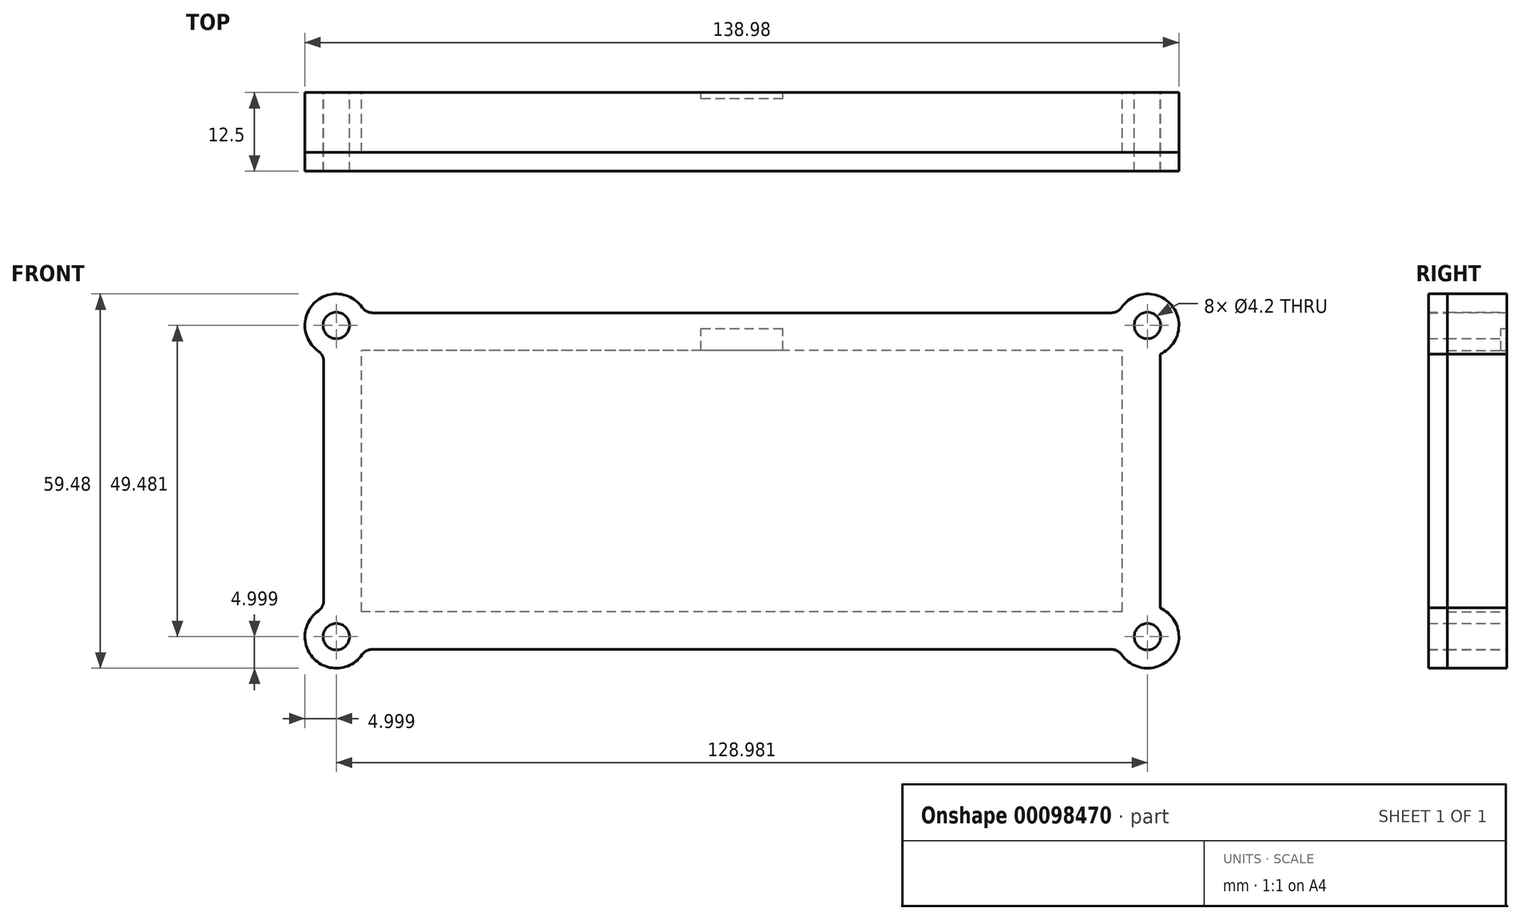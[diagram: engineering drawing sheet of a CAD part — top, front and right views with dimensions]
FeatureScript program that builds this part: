
annotation { "Feature Type Name" : "Feature", "Feature Type Description" : "" }
export const myFeature = defineFeature(function(context is Context, id is Id, definition is map)
    precondition{}
    {
        {
            var Q0;
            Q0=qCreatedBy(makeId("Front.planeOp"),FACE);
            var sketch = newSketch(context, id + "F0", { "sketchPlane" : qUnion([Q0])});
            skLineSegment(sketch, "E0.bottom", {"start": v(60.5, -20.75) * mm, "end": v(-60.5, -20.75) * mm});
            skLineSegment(sketch, "E0.top", {"start": v(60.5, 20.75) * mm, "end": v(-60.5, 20.75) * mm});
            skLineSegment(sketch, "E0.left", {"start": v(60.5, -20.75) * mm, "end": v(60.5, 20.75) * mm});
            skLineSegment(sketch, "E0.right", {"start": v(-60.5, -20.75) * mm, "end": v(-60.5, 20.75) * mm});
            skPoint(sketch, "E0.middle", {"position": v(0, 0) * mm});
            skLineSegment(sketch, "E1.bottom", {"start": v(56.25, 22.8) * mm, "end": v(-56.25, 22.8) * mm, "construction": true});
            skLineSegment(sketch, "E1.top", {"start": v(56.25, -22.8) * mm, "end": v(-56.25, -22.8) * mm, "construction": true});
            skLineSegment(sketch, "E1.left", {"start": v(56.25, 22.8) * mm, "end": v(56.25, -22.8) * mm, "construction": true});
            skLineSegment(sketch, "E1.right", {"start": v(-56.25, 22.8) * mm, "end": v(-56.25, -22.8) * mm, "construction": true});
            skCircle(sketch, "E2", {"center": v(-56.25, 22.8) * mm, "radius": 1 * mm, "construction": true});
            skCircle(sketch, "E3.MirrorC", {"center": v(-56.25, -22.8) * mm, "radius": 1 * mm, "construction": true});
            skCircle(sketch, "E4.MirrorC", {"center": v(56.25, 22.8) * mm, "radius": 1 * mm, "construction": true});
            skCircle(sketch, "E5.MirrorC", {"center": v(56.25, -22.8) * mm, "radius": 1 * mm, "construction": true});
            skLineSegment(sketch, "E6.0", {"start": v(59.91, 26.75) * mm, "end": v(-59.91, 26.75) * mm});
            skLineSegment(sketch, "E6.1", {"start": v(66.5, -20.16) * mm, "end": v(66.5, 20.16) * mm});
            skLineSegment(sketch, "E6.2", {"start": v(59.91, -26.75) * mm, "end": v(-59.91, -26.75) * mm});
            skLineSegment(sketch, "E6.3", {"start": v(-66.5, -20.16) * mm, "end": v(-66.5, 20.16) * mm});
            skLineSegment(sketch, "E7", {"start": v(-66.5, 26.75) * mm, "end": v(-60.5, 20.75) * mm, "construction": true});
            skArc(sketch, "E8", {"start": v(-59.91, 26.75) * mm, "mid": v(-68.03, 28.28) * mm, "end": v(-66.5, 20.16) * mm});
            skCircle(sketch, "E9", {"center": v(-64.5, 24.74) * mm, "radius": 2.1 * mm});
            skArc(sketch, "E10.MirrorCS", {"start": v(59.91, 26.75) * mm, "mid": v(68.03, 28.28) * mm, "end": v(66.5, 20.16) * mm});
            skCircle(sketch, "E11.MirrorC", {"center": v(64.5, 24.74) * mm, "radius": 2.1 * mm});
            skArc(sketch, "E12.MirrorCS", {"start": v(-59.91, -26.75) * mm, "mid": v(-68.03, -28.28) * mm, "end": v(-66.5, -20.16) * mm});
            skCircle(sketch, "E13.MirrorC", {"center": v(-64.5, -24.74) * mm, "radius": 2.1 * mm});
            skArc(sketch, "E14.MirrorCS", {"start": v(59.91, -26.75) * mm, "mid": v(68.03, -28.28) * mm, "end": v(66.5, -20.16) * mm});
            skCircle(sketch, "E15.MirrorC", {"center": v(64.5, -24.74) * mm, "radius": 2.1 * mm});
            skSolve(sketch);
        }
        {
            var Q0;
            Q0 = qSketchRegion(id + "F0", true);
            extrude(context, id + "F1", {"entities" : qUnion([Q0]), "depth" : 9.5 * mm});
        }
        {
            var Q0;
            Q0=makeQuery(id+"F1.opExtrude","SWEPT_EDGE",EDGE,{"disambiguationData":[OSD([sQuery(id+"F0.wireOp",EDGE,"E6.0"),sQuery(id+"F0.wireOp",EDGE,"E8")])]});
            var Q1;
            Q1=makeQuery(id+"F1.opExtrude","SWEPT_EDGE",EDGE,{"disambiguationData":[OSD([sQuery(id+"F0.wireOp",EDGE,"E6.3"),sQuery(id+"F0.wireOp",EDGE,"E8")])]});
            var Q2;
            Q2=makeQuery(id+"F1.opExtrude","SWEPT_EDGE",EDGE,{"disambiguationData":[OSD([sQuery(id+"F0.wireOp",EDGE,"E6.3"),sQuery(id+"F0.wireOp",EDGE,"E12.MirrorCS")])]});
            var Q3;
            Q3=makeQuery(id+"F1.opExtrude","SWEPT_EDGE",EDGE,{"disambiguationData":[OSD([sQuery(id+"F0.wireOp",EDGE,"E6.2"),sQuery(id+"F0.wireOp",EDGE,"E12.MirrorCS")])]});
            var Q4;
            Q4=makeQuery(id+"F1.opExtrude","SWEPT_EDGE",EDGE,{"disambiguationData":[OSD([sQuery(id+"F0.wireOp",EDGE,"E6.2"),sQuery(id+"F0.wireOp",EDGE,"E14.MirrorCS")])]});
            var Q5;
            Q5=makeQuery(id+"F1.opExtrude","SWEPT_EDGE",EDGE,{"disambiguationData":[OSD([sQuery(id+"F0.wireOp",EDGE,"E6.0"),sQuery(id+"F0.wireOp",EDGE,"E10.MirrorCS")])]});
            fillet(context, id + "F2", {"entities" : qUnion([Q0, Q1, Q2, Q3, Q4, Q5]), "radius" : 2 * mm, "tangentPropagation" : true, "allowEdgeOverflow" : false});
        }
        {
            var Q0;
            Q0=makeQuery(id+"F1.opExtrude","CAP_FACE",FACE,{"disambiguationData":[OSD([sQuery(id+"F0.wireOp",EDGE,"E0.bottom"),sQuery(id+"F0.wireOp",EDGE,"E0.top"),sQuery(id+"F0.wireOp",EDGE,"E0.left"),sQuery(id+"F0.wireOp",EDGE,"E0.right"),sQuery(id+"F0.wireOp",EDGE,"E2"),sQuery(id+"F0.wireOp",EDGE,"E3.MirrorC"),sQuery(id+"F0.wireOp",EDGE,"E4.MirrorC"),sQuery(id+"F0.wireOp",EDGE,"E5.MirrorC"),sQuery(id+"F0.wireOp",EDGE,"E6.0"),sQuery(id+"F0.wireOp",EDGE,"E6.1"),sQuery(id+"F0.wireOp",EDGE,"E6.2"),sQuery(id+"F0.wireOp",EDGE,"E6.3"),sQuery(id+"F0.wireOp",EDGE,"E8"),sQuery(id+"F0.wireOp",EDGE,"E9"),sQuery(id+"F0.wireOp",EDGE,"E10.MirrorCS"),sQuery(id+"F0.wireOp",EDGE,"E11.MirrorC"),sQuery(id+"F0.wireOp",EDGE,"E12.MirrorCS"),sQuery(id+"F0.wireOp",EDGE,"E13.MirrorC"),sQuery(id+"F0.wireOp",EDGE,"E14.MirrorCS"),sQuery(id+"F0.wireOp",EDGE,"E15.MirrorC")])],"isStart":true});
            var sketch = newSketch(context, id + "F3", { "sketchPlane" : qUnion([Q0])});
            skLineSegment(sketch, "E16.1", {"start": v(-6.5, 20.75) * mm, "end": v(6.5, 20.75) * mm});
            skLineSegment(sketch, "E17.bottom", {"start": v(0, 20.75) * mm, "end": v(6.5, 20.75) * mm});
            skLineSegment(sketch, "E17.top", {"start": v(0, 24.25) * mm, "end": v(6.5, 24.25) * mm});
            skLineSegment(sketch, "E17.left", {"start": v(0, 20.75) * mm, "end": v(0, 24.25) * mm});
            skLineSegment(sketch, "E17.right", {"start": v(6.5, 20.75) * mm, "end": v(6.5, 24.25) * mm});
            skLineSegment(sketch, "E18.MirrorCS", {"start": v(0, 24.25) * mm, "end": v(-6.5, 24.25) * mm});
            skLineSegment(sketch, "E19.MirrorCS", {"start": v(-6.5, 20.75) * mm, "end": v(-6.5, 24.25) * mm});
            skLineSegment(sketch, "E20.MirrorCS", {"start": v(0, 20.75) * mm, "end": v(-6.5, 20.75) * mm});
            skPoint(sketch, "E16.0.end.orphan", {"position": v(58.75, 26.75) * mm});
            skPoint(sketch, "E16.0.start.orphan", {"position": v(-58.75, 26.75) * mm});
            skPoint(sketch, "E21.orphan", {"position": v(-60.5, 20.75) * mm});
            skPoint(sketch, "E22.orphan", {"position": v(60.5, 20.75) * mm});
            skSolve(sketch);
        }
        {
            var Q0;
            Q0 = qSketchRegion(id + "F3", true);
            extrude(context, id + "F4", {"entities" : qUnion([Q0]), "operationType" : NewBodyOperationType.REMOVE, "oppositeDirection" : true, "depth" : 1 * mm});
        }
        {
            var Q0;
            Q0=makeQuery(id+"F1.opExtrude","CAP_FACE",FACE,{"disambiguationData":[OSD([sQuery(id+"F0.wireOp",EDGE,"E0.bottom"),sQuery(id+"F0.wireOp",EDGE,"E0.top"),sQuery(id+"F0.wireOp",EDGE,"E0.left"),sQuery(id+"F0.wireOp",EDGE,"E0.right"),sQuery(id+"F0.wireOp",EDGE,"E6.0"),sQuery(id+"F0.wireOp",EDGE,"E6.1"),sQuery(id+"F0.wireOp",EDGE,"E6.2"),sQuery(id+"F0.wireOp",EDGE,"E6.3"),sQuery(id+"F0.wireOp",EDGE,"E8"),sQuery(id+"F0.wireOp",EDGE,"E9"),sQuery(id+"F0.wireOp",EDGE,"E10.MirrorCS"),sQuery(id+"F0.wireOp",EDGE,"E11.MirrorC"),sQuery(id+"F0.wireOp",EDGE,"E12.MirrorCS"),sQuery(id+"F0.wireOp",EDGE,"E13.MirrorC"),sQuery(id+"F0.wireOp",EDGE,"E14.MirrorCS"),sQuery(id+"F0.wireOp",EDGE,"E15.MirrorC")])],"isStart":false});
            cPlane(context, id + "F5", {"entities" : qUnion([Q0]), "cplaneType" : CPlaneType.OFFSET, "offset" : 0 * mm, "width" : 150 * mm, "height" : 150 * mm});
        }
        {
            var Q0;
            Q0=qCreatedBy(id+"F5.planeOp",FACE);
            var sketch = newSketch(context, id + "F6", { "sketchPlane" : qUnion([Q0])});
            skArc(sketch, "E23.0.0", {"start": v(66.5, 20.16) * mm, "mid": v(68.36, 27.91) * mm, "end": v(60.4, 27.6) * mm});
            skArc(sketch, "E23.0.1", {"start": v(60.4, 27.6) * mm, "mid": v(59.68, 26.98) * mm, "end": v(58.75, 26.75) * mm});
            skLineSegment(sketch, "E23.0.2", {"start": v(58.75, 26.75) * mm, "end": v(-58.75, 26.75) * mm});
            skArc(sketch, "E23.0.3", {"start": v(-58.75, 26.75) * mm, "mid": v(-59.68, 26.98) * mm, "end": v(-60.4, 27.6) * mm});
            skArc(sketch, "E23.0.4", {"start": v(-60.4, 27.6) * mm, "mid": v(-68.03, 28.28) * mm, "end": v(-67.35, 20.64) * mm});
            skArc(sketch, "E23.0.5", {"start": v(-67.35, 20.64) * mm, "mid": v(-66.73, 19.93) * mm, "end": v(-66.5, 19) * mm});
            skLineSegment(sketch, "E23.0.6", {"start": v(-66.5, 19) * mm, "end": v(-66.5, -19) * mm});
            skArc(sketch, "E23.0.7", {"start": v(-66.5, -19) * mm, "mid": v(-66.73, -19.93) * mm, "end": v(-67.35, -20.64) * mm});
            skArc(sketch, "E23.0.8", {"start": v(-67.35, -20.64) * mm, "mid": v(-68.03, -28.28) * mm, "end": v(-60.4, -27.6) * mm});
            skArc(sketch, "E23.0.9", {"start": v(-60.4, -27.6) * mm, "mid": v(-59.68, -26.98) * mm, "end": v(-58.75, -26.75) * mm});
            skLineSegment(sketch, "E23.0.10", {"start": v(-58.75, -26.75) * mm, "end": v(58.75, -26.75) * mm});
            skArc(sketch, "E23.0.11", {"start": v(58.75, -26.75) * mm, "mid": v(59.68, -26.98) * mm, "end": v(60.4, -27.6) * mm});
            skArc(sketch, "E23.0.12", {"start": v(60.4, -27.6) * mm, "mid": v(68.36, -27.91) * mm, "end": v(66.5, -20.16) * mm});
            skLineSegment(sketch, "E23.0.13", {"start": v(66.5, -20.16) * mm, "end": v(66.5, 20.16) * mm});
            skCircle(sketch, "E24.0", {"center": v(-64.5, 24.74) * mm, "radius": 2.1 * mm});
            skCircle(sketch, "E24.1", {"center": v(-64.5, -24.74) * mm, "radius": 2.1 * mm});
            skCircle(sketch, "E24.2", {"center": v(64.5, 24.74) * mm, "radius": 2.1 * mm});
            skCircle(sketch, "E24.3", {"center": v(64.5, -24.74) * mm, "radius": 2.1 * mm});
            skSolve(sketch);
        }
        {
            var Q0;
            Q0 = qSketchRegion(id + "F6", true);
            extrude(context, id + "F7", {"entities" : qUnion([Q0]), "depth" : 3 * mm});
        }
    });
